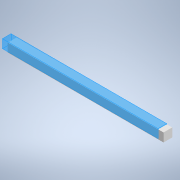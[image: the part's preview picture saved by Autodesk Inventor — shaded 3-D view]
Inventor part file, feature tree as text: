
AUTODESK INVENTOR PART (.ipt)
format: ipt  version: 2022 (Build 260153000, 153)  size: 93,696 bytes
history: native  units: in
note: dims shown in document units (in); Inventor stores cm internally (conversion verified against a paired STEP export)
features: extrude x1, sketch x1
ambient origin geometry x8: Origin, YZ Plane, XZ Plane, XY Plane, X Axis, Y Axis, Z Axis, Center Point
bodies: Solid1 (feature_tree)
feature tree (2):
  extrude  "Extrusion1"  Depth=1.0in
  sketch  "Sketch1"  dims[d0=18.0in d1=1.0in d2=1.0in d3=0.0in]
